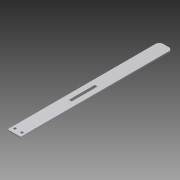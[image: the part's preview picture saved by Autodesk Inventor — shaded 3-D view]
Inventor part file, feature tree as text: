
AUTODESK INVENTOR PART (.ipt)
format: ipt  version: 2015 (Build 190159000, 159)  size: 132,608 bytes
history: native  units: mm
features: sketch x4, extrude x3, other x1, fillet x1, hole x1
ambient origin geometry x8: Origin, YZ Plane, XZ Plane, XY Plane, X Axis, Y Axis, Z Axis, Center Point
bodies: Body1 (feature_tree)
feature tree (10):
  other  "ソリッド1"
  extrude  "押し出し1"  Depth=15.0mm
  extrude  "押し出し2"  Depth=166.0mm
  fillet  "フィレット1"  Radius=1.5mm
  extrude  "押し出し4"  Depth=3.1mm
  hole  "穴2"  [1 undecoded]
  sketch  "スケッチ1"
  sketch  "スケッチ2"
  sketch  "スケッチ5"
  sketch  "スケッチ6"
note: 1 required parameter value undecoded (feature->parameter linkage not recoverable at this tier; creation-order binding heuristic only, values carry confidence <= 0.55)
